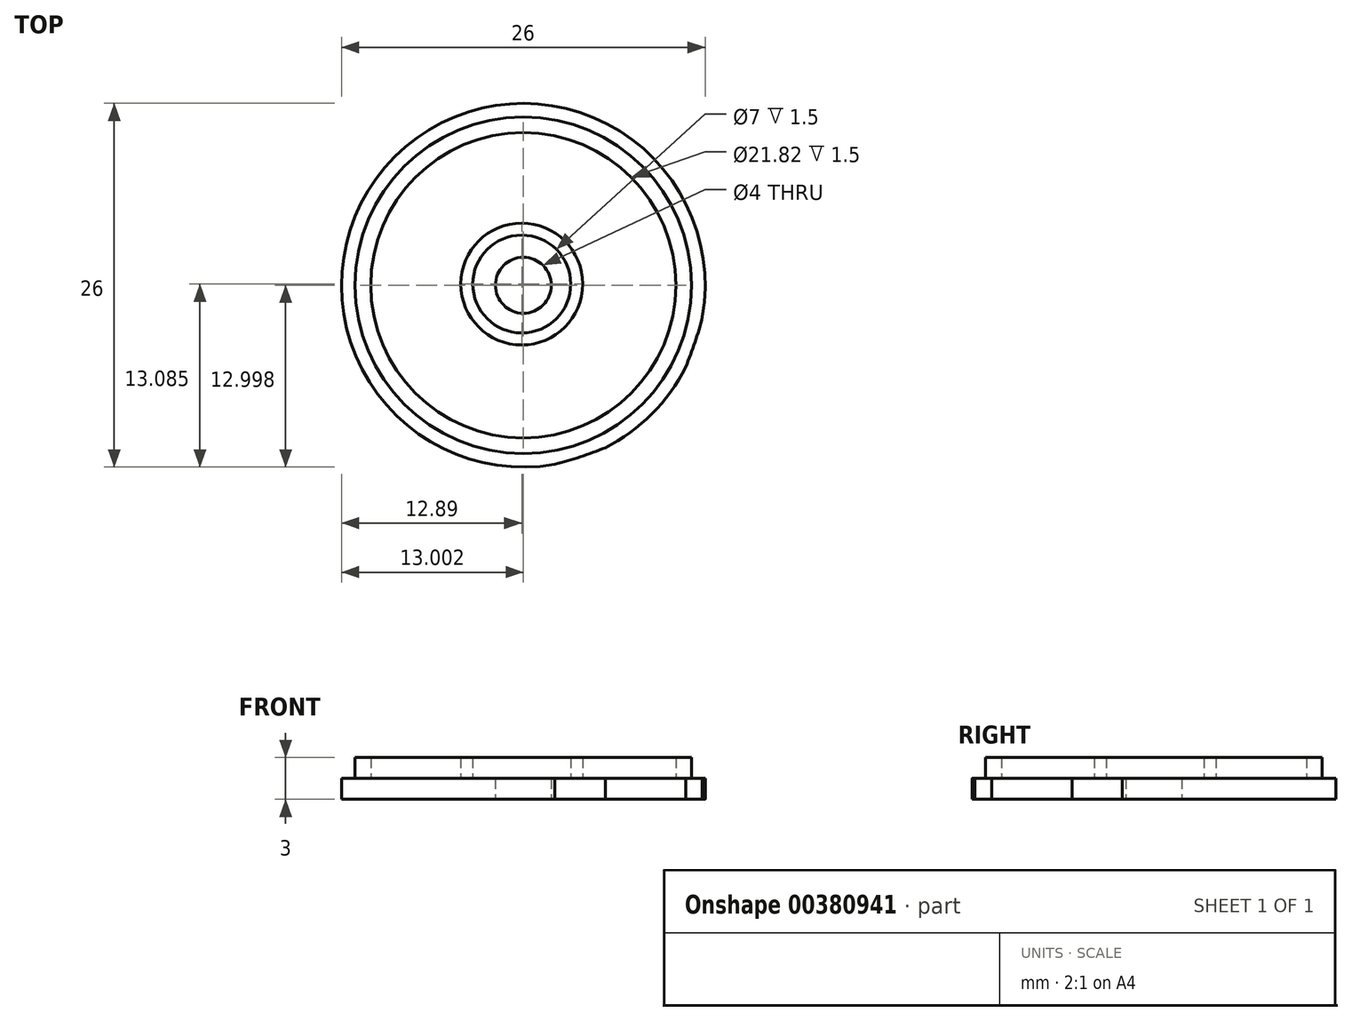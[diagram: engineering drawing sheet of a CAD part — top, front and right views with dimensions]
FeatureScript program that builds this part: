
annotation { "Feature Type Name" : "Feature", "Feature Type Description" : "" }
export const myFeature = defineFeature(function(context is Context, id is Id, definition is map)
    precondition{}
    {
        {
            var Q0;
            Q0=qCreatedBy(makeId("Top.planeOp"),FACE);
            var sketch = newSketch(context, id + "F0", { "sketchPlane" : qUnion([Q0])});
            skArc(sketch, "E0.3.1", {"start": v(10.48, 0.06) * mm, "mid": v(-11.51, 11.51) * mm, "end": v(-0.06, -10.48) * mm});
            skArc(sketch, "E1.trimOffspring", {"start": v(3.53, -9.3) * mm, "mid": v(6.87, -6.87) * mm, "end": v(9.3, -3.53) * mm});
            skArc(sketch, "E2", {"start": v(9.3, -3.53) * mm, "mid": v(9.96, -1.76) * mm, "end": v(10.48, 0.06) * mm});
            skArc(sketch, "E3", {"start": v(-0.06, -10.48) * mm, "mid": v(1.76, -9.95) * mm, "end": v(3.53, -9.3) * mm});
            skCircle(sketch, "E4.1.0", {"center": v(-2.43, 2.4) * mm, "radius": 4.36 * mm});
            skCircle(sketch, "E4.1.2", {"center": v(-2.43, 2.4) * mm, "radius": 3.5 * mm});
            skCircle(sketch, "E4.1.3", {"center": v(-2.43, 2.4) * mm, "radius": 10 * mm});
            skCircle(sketch, "E5", {"center": v(-2.32, 2.32) * mm, "radius": 2 * mm});
            skCircle(sketch, "E6.2.0", {"center": v(-2.32, 2.32) * mm, "radius": 10.9 * mm});
            skCircle(sketch, "E6.2.1", {"center": v(-2.32, 2.32) * mm, "radius": 12.03 * mm});
            skSolve(sketch);
        }
        {
            var Q0;
            Q0 = qSketchRegion(id + "F0", true);
            var Q1;
            Q1=makeQuery(id+"F0.imprint","IMPRINT",FACE,{"disambiguationData":[TD([[makeQuery(id+"F0.imprint","IMPRINT",EDGE,{"derivedFrom":sQuery(id+"F0.wireOp",EDGE,"E4.1.0")}),-1.0]])]});
            var Q2;
            Q2=makeQuery(id+"F0.imprint","IMPRINT",FACE,{"disambiguationData":[TD([[makeQuery(id+"F0.imprint","IMPRINT",EDGE,{"derivedFrom":sQuery(id+"F0.wireOp",EDGE,"E4.1.2")}),1.0]])]});
            var Q3;
            Q3=makeQuery(id+"F0.imprint","IMPRINT",FACE,{"disambiguationData":[TD([[makeQuery(id+"F0.imprint","IMPRINT",EDGE,{"derivedFrom":sQuery(id+"F0.wireOp",EDGE,"E5")}),1.0]])]});
            var Q4;
            Q4=makeQuery(id+"F0.imprint","IMPRINT",FACE,{"disambiguationData":[TD([[makeQuery(id+"F0.imprint","IMPRINT",EDGE,{"derivedFrom":sQuery(id+"F0.wireOp",EDGE,"E4.1.0")}),1.0]])]});
            var Q5;
            Q5=makeQuery(id+"F0.imprint","IMPRINT",FACE,{"disambiguationData":[TD([[makeQuery(id+"F0.imprint","IMPRINT",EDGE,{"derivedFrom":sQuery(id+"F0.wireOp",EDGE,"E4.1.3")}),-1.0]])]});
            var Q6;
            Q6=makeQuery(id+"F0.imprint","IMPRINT",FACE,{"disambiguationData":[TD([[makeQuery(id+"F0.imprint","IMPRINT",EDGE,{"derivedFrom":sQuery(id+"F0.wireOp",EDGE,"E6.2.0")}),-1.0]])]});
            extrude(context, id + "F1", {"entities" : qUnion([Q0, Q1, Q2, Q3, Q4, Q5, Q6]), "depth" : 1.5 * mm});
        }
        {
            var Q0;
            Q0=makeQuery(id+"F0.imprint","IMPRINT",FACE,{"disambiguationData":[TD([[makeQuery(id+"F0.imprint","IMPRINT",EDGE,{"derivedFrom":sQuery(id+"F0.wireOp",EDGE,"E6.2.0")}),-1.0]])]});
            var Q1;
            Q1=makeQuery(id+"F0.imprint","IMPRINT",FACE,{"disambiguationData":[TD([[makeQuery(id+"F0.imprint","IMPRINT",EDGE,{"derivedFrom":sQuery(id+"F0.wireOp",EDGE,"E4.1.0")}),1.0]])]});
            extrude(context, id + "F2", {"entities" : qUnion([Q0, Q1]), "operationType" : NewBodyOperationType.ADD, "depth" : 3 * mm});
        }
        {
            var Q0;
            Q0=makeQuery(id+"F0.imprint","IMPRINT",FACE,{"disambiguationData":[TD([[makeQuery(id+"F0.imprint","IMPRINT",EDGE,{"derivedFrom":sQuery(id+"F0.wireOp",EDGE,"E5")}),1.0]])]});
            extrude(context, id + "F3", {"entities" : qUnion([Q0]), "operationType" : NewBodyOperationType.REMOVE, "depth" : 25.4 * mm});
        }
    });
